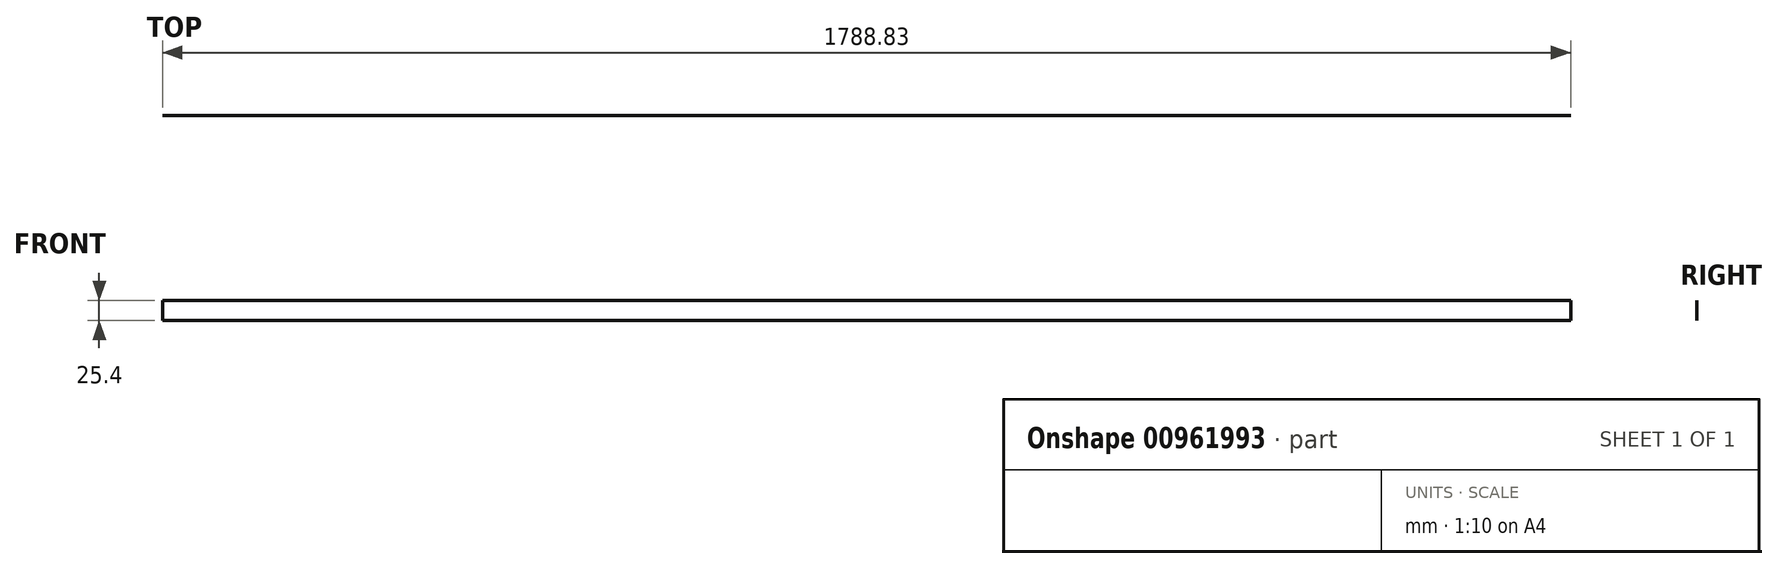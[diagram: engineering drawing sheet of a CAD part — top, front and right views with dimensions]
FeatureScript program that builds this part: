
annotation { "Feature Type Name" : "Feature", "Feature Type Description" : "" }
export const myFeature = defineFeature(function(context is Context, id is Id, definition is map)
    precondition{}
    {
        {
            var Q0;
            Q0=qCreatedBy(makeId("Top.planeOp"),FACE);
            var sketch = newSketch(context, id + "F0", { "sketchPlane" : qUnion([Q0])});
            skLineSegment(sketch, "E0", {"start": v(-888.75, 339.84) * mm, "end": v(900.08, 339.84) * mm});
            skSolve(sketch);
        }
        {
            var Q0;
            Q0=sQuery(id+"F0.wireOp",EDGE,"E0");
            extrude(context, id + "F1", {"bodyType" : ToolBodyType.SURFACE, "surfaceEntities" : qUnion([Q0]), "depth" : 25.4 * mm, "offsetDistance" : 25.4 * mm});
        }
    });
